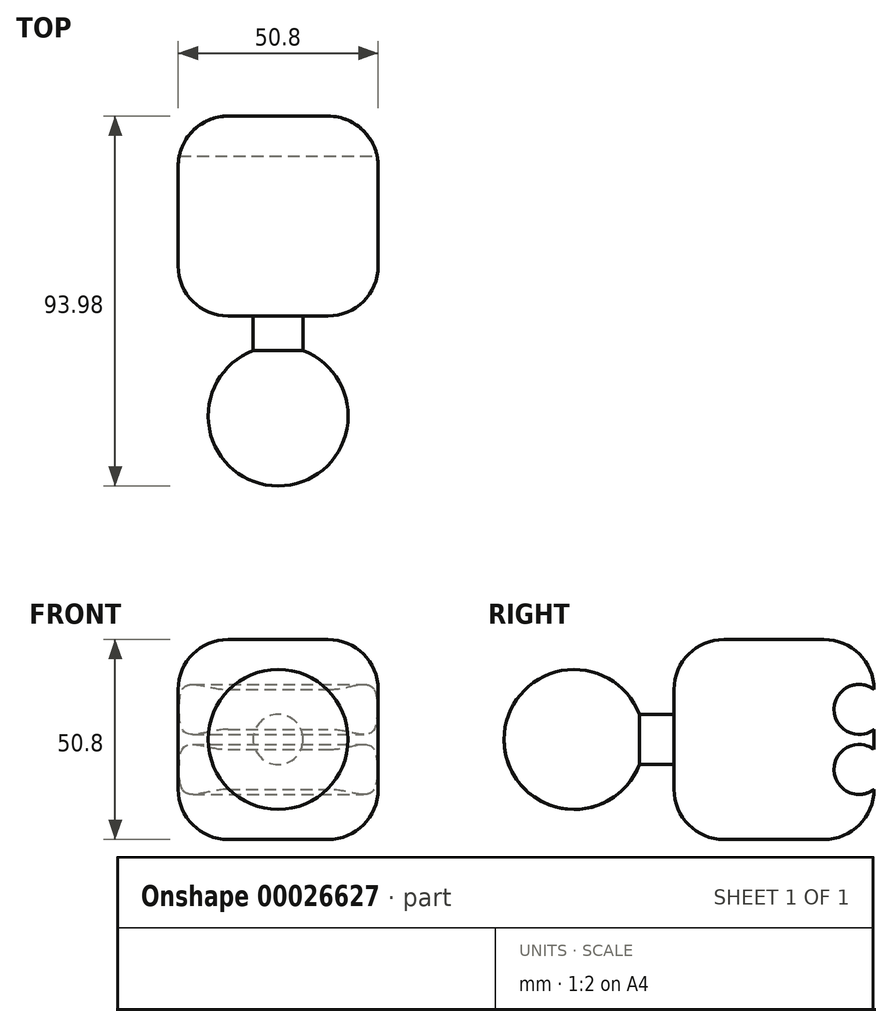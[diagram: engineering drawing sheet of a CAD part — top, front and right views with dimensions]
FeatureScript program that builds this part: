
annotation { "Feature Type Name" : "Feature", "Feature Type Description" : "" }
export const myFeature = defineFeature(function(context is Context, id is Id, definition is map)
    precondition{}
    {
        {
            var Q0;
            Q0=qCreatedBy(makeId("Front.planeOp"),FACE);
            var sketch = newSketch(context, id + "F0", { "sketchPlane" : qUnion([Q0])});
            skLineSegment(sketch, "E0.bottom", {"start": v(0, 0) * mm, "end": v(50.8, 0) * mm});
            skLineSegment(sketch, "E0.top", {"start": v(0, 50.8) * mm, "end": v(50.8, 50.8) * mm});
            skLineSegment(sketch, "E0.left", {"start": v(0, 0) * mm, "end": v(0, 50.8) * mm});
            skLineSegment(sketch, "E0.right", {"start": v(50.8, 0) * mm, "end": v(50.8, 50.8) * mm});
            skSolve(sketch);
        }
        {
            var Q0;
            Q0=qSketchRegion(id+"F0",true);
            extrude(context, id + "F1", {"entities" : qUnion([Q0]), "depth" : 50.8 * mm});
        }
        {
            var Q0;
            Q0=makeQuery(id+"F1.opExtrude","SWEPT_FACE",FACE,{"disambiguationData":[OSD([sQuery(id+"F0.wireOp",EDGE,"E0.bottom")])]});
            var Q1;
            Q1=makeQuery(id+"F1.opExtrude","SWEPT_FACE",FACE,{"disambiguationData":[OSD([sQuery(id+"F0.wireOp",EDGE,"E0.left")])]});
            var Q2;
            Q2=makeQuery(id+"F1.opExtrude","SWEPT_FACE",FACE,{"disambiguationData":[OSD([sQuery(id+"F0.wireOp",EDGE,"E0.top")])]});
            var Q3;
            Q3=makeQuery(id+"F1.opExtrude","SWEPT_FACE",FACE,{"disambiguationData":[OSD([sQuery(id+"F0.wireOp",EDGE,"E0.right")])]});
            fillet(context, id + "F2", {"entities" : qUnion([Q0, Q1, Q2, Q3]), "radius" : 12.7 * mm, "tangentPropagation" : true, "allowEdgeOverflow" : false});
        }
        {
            var Q0;
            Q0=makeQuery(id+"F1.opExtrude","SWEPT_FACE",FACE,{"disambiguationData":[OSD([sQuery(id+"F0.wireOp",EDGE,"E0.right")])]});
            var Q1;
            Q1=makeQuery(id+"F1.opExtrude","SWEPT_FACE",FACE,{"disambiguationData":[OSD([sQuery(id+"F0.wireOp",EDGE,"E0.left")])]});
            cPlane(context, id + "F3", {"entities" : qUnion([Q0, Q1]), "cplaneType" : CPlaneType.MID_PLANE, "offset" : 152.4 * mm, "width" : 152.4 * mm, "height" : 152.4 * mm});
        }
        {
            var Q0;
            Q0=makeQuery(id+"F1.opExtrude","CAP_FACE",FACE,{"disambiguationData":[OSD([sQuery(id+"F0.wireOp",EDGE,"E0.bottom"),sQuery(id+"F0.wireOp",EDGE,"E0.top"),sQuery(id+"F0.wireOp",EDGE,"E0.left"),sQuery(id+"F0.wireOp",EDGE,"E0.right")])],"isStart":false});
            var sketch = newSketch(context, id + "F4", { "sketchPlane" : qUnion([Q0])});
            skCircle(sketch, "E1", {"center": v(25.4, 25.4) * mm, "radius": 6.35 * mm});
            skSolve(sketch);
        }
        {
            var Q0;
            Q0=qSketchRegion(id+"F4",true);
            extrude(context, id + "F5", {"entities" : qUnion([Q0]), "operationType" : NewBodyOperationType.ADD, "depth" : 12.7 * mm});
        }
        {
            var Q0;
            Q0=qCreatedBy(id+"F3.planeOp",FACE);
            var sketch = newSketch(context, id + "F6", { "sketchPlane" : qUnion([Q0])});
            skPoint(sketch, "E2", {"position": v(-76.2, 25.4) * mm});
            skArc(sketch, "E3", {"start": v(-93.98, 25.4) * mm, "mid": v(-76.2, 7.62) * mm, "end": v(-58.42, 25.4) * mm});
            skLineSegment(sketch, "E4", {"start": v(-76.2, 25.4) * mm, "end": v(-58.42, 25.4) * mm});
            skLineSegment(sketch, "E5", {"start": v(-76.2, 25.4) * mm, "end": v(-93.98, 25.4) * mm});
            skSolve(sketch);
        }
        {
            var Q0;
            Q0=makeQuery(id+"F6.imprint","IMPRINT",FACE,{"disambiguationData":[TD([[makeQuery(id+"F6.imprint","IMPRINT",EDGE,{"derivedFrom":sQuery(id+"F6.wireOp",EDGE,"E3")}),1.0]])]});
            var Q1;
            Q1=sQuery(id+"F6.wireOp",EDGE,"E5");
            revolve(context, id + "F7", {"operationType" : NewBodyOperationType.ADD, "entities" : qUnion([Q0]), "axis" : qUnion([Q1]), "revolveType" : RevolveType.FULL});
        }
        {
            var Q0;
            Q0=qCreatedBy(id+"F3.planeOp",FACE);
            var sketch = newSketch(context, id + "F8", { "sketchPlane" : qUnion([Q0])});
            skLineSegment(sketch, "E6", {"start": v(-12.56, 38.02) * mm, "end": v(12.84, 38.02) * mm});
            skArc(sketch, "E7", {"start": v(12.84, 38.02) * mm, "mid": v(65.2, 31.57) * mm, "end": v(114.44, 12.62) * mm});
            skLineSegment(sketch, "E8", {"start": v(-12.56, 38.02) * mm, "end": v(-12.56, 50.72) * mm});
            skLineSegment(sketch, "E9", {"start": v(-12.56, 50.72) * mm, "end": v(38.24, 50.72) * mm});
            skArc(sketch, "E10", {"start": v(38.24, 50.72) * mm, "mid": v(80.84, 40.66) * mm, "end": v(114.44, 12.62) * mm});
            skSolve(sketch);
        }
        {
            var Q0;
            Q0=makeQuery(id+"F8.imprint","IMPRINT",FACE,{"disambiguationData":[TD([[makeQuery(id+"F8.imprint","IMPRINT",EDGE,{"derivedFrom":sQuery(id+"F8.wireOp",EDGE,"E6")}),1.0]])]});
            extrude(context, id + "F9", {"entities" : qUnion([Q0]), "depth" : 25.4 * mm, "hasDraft" : true, "draftAngle" : 16 * degree, "draftPullDirection" : true, "hasSecondDirection" : true, "secondDirectionOppositeDirection" : true, "secondDirectionDepth" : 25.4 * mm, "hasSecondDirectionDraft" : true, "secondDirectionDraftAngle" : 16 * degree, "secondDirectionDraftPullDirection" : true});
        }
        {
            var Q0;
            Q0=makeQuery(id+"F9.split0.splitOp","SPLIT",BODY,{"derivedFrom":makeQuery(id+"F9.opExtrude","SWEPT_BODY",BODY,{"disambiguationData":[OSD([sQuery(id+"F8.wireOp",EDGE,"E6"),sQuery(id+"F8.wireOp",EDGE,"E7"),sQuery(id+"F8.wireOp",EDGE,"E8"),sQuery(id+"F8.wireOp",EDGE,"E9"),sQuery(id+"F8.wireOp",EDGE,"E10")])]})});
            deleteBodies(context, id + "F10", {"entities" : qUnion([Q0])});
        }
        {
            var Q0;
            Q0=qCreatedBy(id+"F3.planeOp",FACE);
            var sketch = newSketch(context, id + "F11", { "sketchPlane" : qUnion([Q0])});
            skCircle(sketch, "E11", {"center": v(-3.8, 33.02) * mm, "radius": 6.35 * mm});
            skLineSegment(sketch, "E12", {"start": v(0, 0) * mm, "end": v(0, 50.8) * mm});
            skLineSegment(sketch, "E13", {"start": v(0, 33.02) * mm, "end": v(-3.8, 33.02) * mm});
            skLineSegment(sketch, "E14", {"start": v(0, 25.4) * mm, "end": v(-23.3, 25.4) * mm});
            skCircle(sketch, "E15.MirrorC", {"center": v(-3.8, 17.78) * mm, "radius": 6.35 * mm});
            skSolve(sketch);
        }
        {
            var Q0;
            Q0 = qSketchRegion(id + "F11", true);
            extrude(context, id + "F12", {"entities" : qUnion([Q0]), "operationType" : NewBodyOperationType.REMOVE, "endBound" : BoundingType.THROUGH_ALL, "oppositeDirection" : true, "depth" : 25.4 * mm, "hasSecondDirection" : true, "secondDirectionBound" : BoundingType.THROUGH_ALL, "secondDirectionOppositeDirection" : false, "secondDirectionDepth" : 25.4 * mm});
        }
    });
